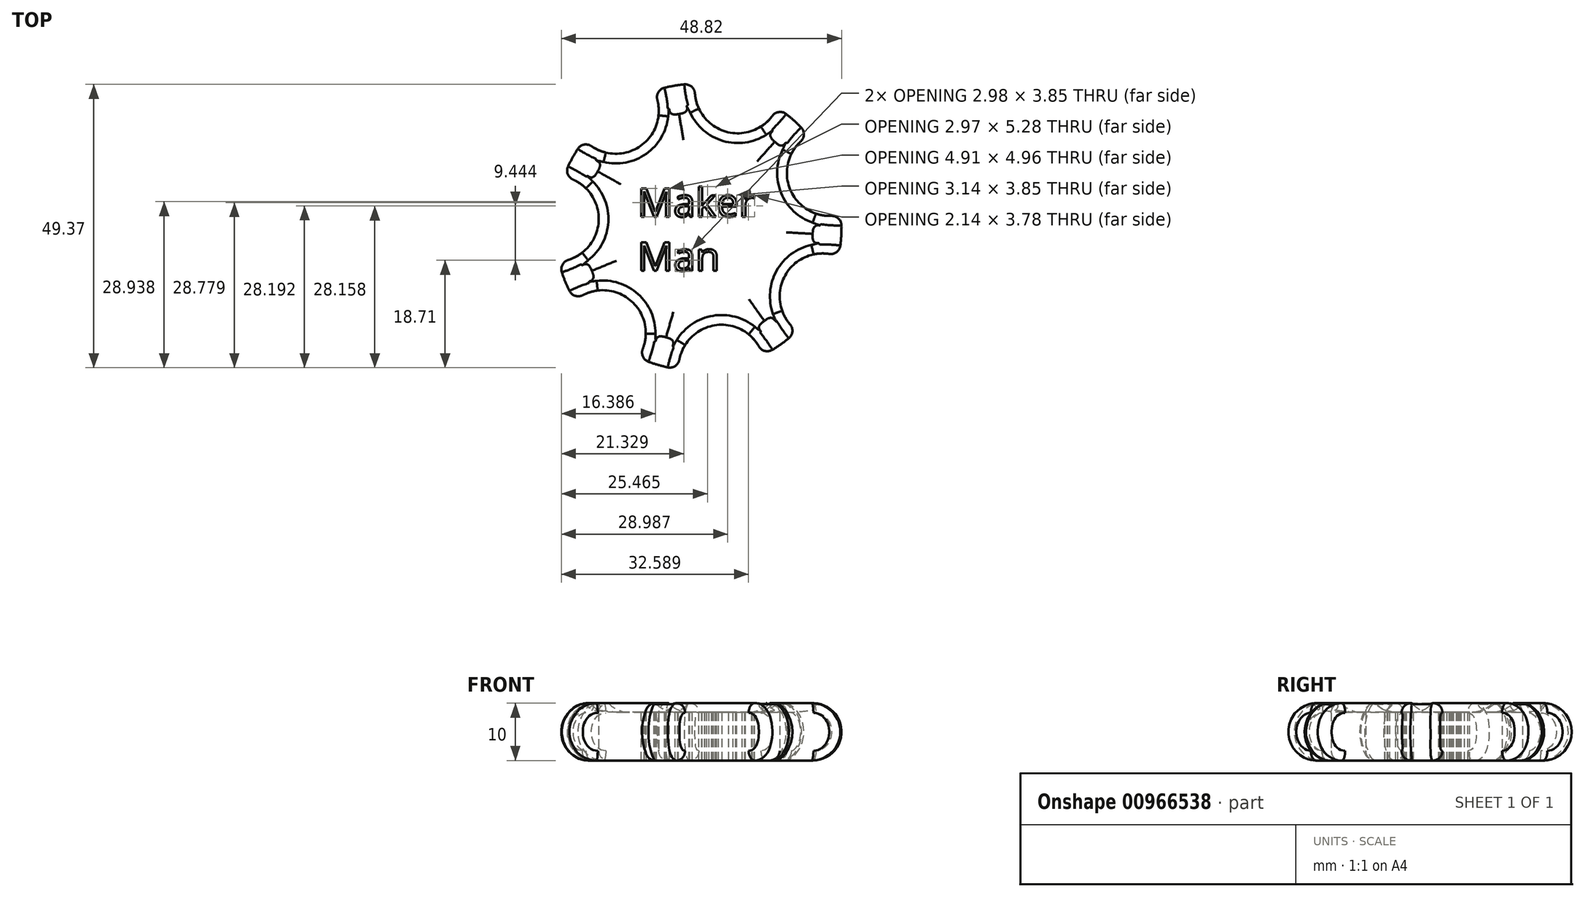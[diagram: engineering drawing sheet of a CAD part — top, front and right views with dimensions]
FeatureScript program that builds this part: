
annotation { "Feature Type Name" : "Feature", "Feature Type Description" : "" }
export const myFeature = defineFeature(function(context is Context, id is Id, definition is map)
    precondition{}
    {
        {
            var Q0;
            Q0=qCreatedBy(makeId("Top.planeOp"),FACE);
            var sketch = newSketch(context, id + "F0", { "sketchPlane" : qUnion([Q0])});
            skCircle(sketch, "E0", {"center": v(0, 0) * mm, "radius": 25 * mm});
            skSolve(sketch);
        }
        {
            var Q0;
            Q0=makeQuery(id+"F0.imprint","IMPRINT",FACE,{"disambiguationData":[TD([[makeQuery(id+"F0.imprint","IMPRINT",EDGE,{"derivedFrom":sQuery(id+"F0.wireOp",EDGE,"E0")}),1.0]])]});
            extrude(context, id + "F1", {"entities" : qUnion([Q0]), "depth" : 10 * mm, "offsetDistance" : 25 * mm});
        }
        {
            var Q0;
            Q0=makeQuery(id+"F1.opExtrude","CAP_EDGE",EDGE,{"disambiguationData":[OSD([sQuery(id+"F0.wireOp",EDGE,"E0")])],"isStart":false});
            var Q1;
            Q1=makeQuery(id+"F1.opExtrude","CAP_EDGE",EDGE,{"disambiguationData":[OSD([sQuery(id+"F0.wireOp",EDGE,"E0")])],"isStart":true});
            fillet(context, id + "F2", {"entities" : qUnion([Q0, Q1]), "radius" : 5 * mm, "tangentPropagation" : true, "allowEdgeOverflow" : false});
        }
        {
            var Q0;
            Q0=qCreatedBy(makeId("Top.planeOp"),FACE);
            var sketch = newSketch(context, id + "F3", { "sketchPlane" : qUnion([Q0])});
            skArc(sketch, "E1", {"start": v(0, 26.67) * mm, "mid": v(5.1, 16.59) * mm, "end": v(14.37, 23.07) * mm});
            skLineSegment(sketch, "E2", {"start": v(14.37, 23.07) * mm, "end": v(0, 26.67) * mm});
            skLineSegment(sketch, "E3.1.0", {"start": v(-9.07, 25.62) * mm, "end": v(-20.85, 16.63) * mm});
            skArc(sketch, "E3.1.1", {"start": v(-20.85, 16.63) * mm, "mid": v(-9.78, 14.33) * mm, "end": v(-9.07, 25.62) * mm});
            skLineSegment(sketch, "E3.2.0", {"start": v(-25.69, 8.88) * mm, "end": v(-26, -5.94) * mm});
            skArc(sketch, "E3.2.1", {"start": v(-26, -5.94) * mm, "mid": v(-17.3, 1.29) * mm, "end": v(-25.69, 8.88) * mm});
            skLineSegment(sketch, "E3.3.0", {"start": v(-22.96, -14.54) * mm, "end": v(-11.57, -24.03) * mm});
            skArc(sketch, "E3.3.1", {"start": v(-11.57, -24.03) * mm, "mid": v(-11.8, -12.73) * mm, "end": v(-22.96, -14.54) * mm});
            skLineSegment(sketch, "E3.4.0", {"start": v(-2.94, -27.02) * mm, "end": v(11.57, -24.03) * mm});
            skArc(sketch, "E3.4.1", {"start": v(11.57, -24.03) * mm, "mid": v(2.6, -17.16) * mm, "end": v(-2.94, -27.02) * mm});
            skLineSegment(sketch, "E3.5.0", {"start": v(19.29, -19.15) * mm, "end": v(26, -5.94) * mm});
            skArc(sketch, "E3.5.1", {"start": v(26, -5.94) * mm, "mid": v(15.03, -8.67) * mm, "end": v(19.29, -19.15) * mm});
            skLineSegment(sketch, "E3.6.0", {"start": v(27, 3.14) * mm, "end": v(20.85, 16.63) * mm});
            skArc(sketch, "E3.6.1", {"start": v(20.85, 16.63) * mm, "mid": v(16.15, 6.35) * mm, "end": v(27, 3.14) * mm});
            skPoint(sketch, "E3.center", {"position": v(0, 0) * mm});
            skSolve(sketch);
        }
        {
            var Q0;
            Q0=makeQuery(id+"F3.imprint","IMPRINT",FACE,{"disambiguationData":[TD([[makeQuery(id+"F3.imprint","IMPRINT",EDGE,{"derivedFrom":sQuery(id+"F3.wireOp",EDGE,"E1")}),1.0]])]});
            extrude(context, id + "F4", {"entities" : qUnion([Q0]), "operationType" : NewBodyOperationType.REMOVE, "depth" : 27.2 * mm, "offsetDistance" : 25 * mm});
        }
        {
            var Q0;
            Q0 = qSketchRegion(id + "F3", true);
            extrude(context, id + "F5", {"entities" : qUnion([Q0]), "operationType" : NewBodyOperationType.REMOVE, "depth" : 25 * mm, "offsetDistance" : 25 * mm});
        }
        {
            var Q0;
            Q0=makeQuery(id+"F4.boolean.opBoolean","COPY",FACE,{"derivedFrom":makeQuery(id+"F4.opExtrude","SWEPT_FACE",FACE,{"disambiguationData":[OSD([sQuery(id+"F3.wireOp",EDGE,"E1")])]})});
            var Q1;
            Q1=makeQuery(id+"F5.boolean.opBoolean","COPY",FACE,{"derivedFrom":makeQuery(id+"F5.opExtrude","SWEPT_FACE",FACE,{"disambiguationData":[OSD([sQuery(id+"F3.wireOp",EDGE,"E3.6.1")])]})});
            var Q2;
            Q2=makeQuery(id+"F5.boolean.opBoolean","COPY",FACE,{"derivedFrom":makeQuery(id+"F5.opExtrude","SWEPT_FACE",FACE,{"disambiguationData":[OSD([sQuery(id+"F3.wireOp",EDGE,"E3.5.1")])]})});
            var Q3;
            Q3=makeQuery(id+"F5.boolean.opBoolean","COPY",FACE,{"derivedFrom":makeQuery(id+"F5.opExtrude","SWEPT_FACE",FACE,{"disambiguationData":[OSD([sQuery(id+"F3.wireOp",EDGE,"E3.4.1")])]})});
            var Q4;
            Q4=makeQuery(id+"F5.boolean.opBoolean","COPY",FACE,{"derivedFrom":makeQuery(id+"F5.opExtrude","SWEPT_FACE",FACE,{"disambiguationData":[OSD([sQuery(id+"F3.wireOp",EDGE,"E3.3.1")])]})});
            var Q5;
            Q5=makeQuery(id+"F5.boolean.opBoolean","COPY",FACE,{"derivedFrom":makeQuery(id+"F5.opExtrude","SWEPT_FACE",FACE,{"disambiguationData":[OSD([sQuery(id+"F3.wireOp",EDGE,"E3.2.1")])]})});
            var Q6;
            Q6=makeQuery(id+"F5.boolean.opBoolean","COPY",FACE,{"derivedFrom":makeQuery(id+"F5.opExtrude","SWEPT_FACE",FACE,{"disambiguationData":[OSD([sQuery(id+"F3.wireOp",EDGE,"E3.1.1")])]})});
            fillet(context, id + "F6", {"entities" : qUnion([Q0, Q1, Q2, Q3, Q4, Q5, Q6]), "radius" : 1.69 * mm, "tangentPropagation" : true, "allowEdgeOverflow" : false});
        }
        {
            var Q0;
            Q0=makeQuery(id+"F1.opExtrude","CAP_FACE",FACE,{"disambiguationData":[OSD([sQuery(id+"F0.wireOp",EDGE,"E0")])],"isStart":false});
            extrude(context, id + "F7", {"entities" : qUnion([Q0]), "operationType" : NewBodyOperationType.REMOVE, "oppositeDirection" : true, "depth" : 1.6 * mm, "offsetDistance" : 25 * mm});
        }
        {
            var Q0;
            Q0=makeQuery(id+"F7.boolean.opBoolean","COPY",FACE,{"derivedFrom":makeQuery(id+"F7.opExtrude","CAP_FACE",FACE,{"disambiguationData":[OSD([sQuery(id+"F0.wireOp",EDGE,"E0")])],"isStart":false})});
            fillet(context, id + "F8", {"entities" : qUnion([Q0]), "radius" : 5 * mm, "tangentPropagation" : true, "allowEdgeOverflow" : false});
        }
        {
            var Q0;
            {var subQ0=sQuery(id+"F0.wireOp",EDGE,"E0");var subQ1=makeQuery(id+"F1.opExtrude","CAP_FACE",FACE,{"disambiguationData":[OSD([subQ0])],"isStart":false});var subQ2=makeQuery(id+"F5.boolean.opBoolean","SPLIT",EDGE,{"disambiguationData":[TD([subQ1,makeQuery(id+"F2.opFillet","BLEND_FACE",FACE,{"disambiguationData":[OSD([subQ0])]}),makeQuery(id+"F4.boolean.opBoolean","COPY",FACE,{"derivedFrom":makeQuery(id+"F4.opExtrude","SWEPT_FACE",FACE,{"disambiguationData":[OSD([sQuery(id+"F3.wireOp",EDGE,"E1")])]})}),makeQuery(id+"F5.opExtrude","SWEPT_FACE",FACE,{"disambiguationData":[OSD([sQuery(id+"F3.wireOp",EDGE,"E3.1.1")])]})])],"derivedFrom":makeQuery(id+"F2.opFillet","BLEND_EDGE",EDGE,{"blendedFrom":[makeQuery(id+"F1.opExtrude","CAP_EDGE",EDGE,{"disambiguationData":[OSD([subQ0])],"isStart":false}),subQ1],"blendedInto":[subQ1]})});Q0=makeQuery(id+"F7.boolean.opBoolean","MERGE",EDGE,{"derivedFrom":[subQ2],"fromTools":[makeQuery(id+"F7.opExtrude","CAP_EDGE",EDGE,{"disambiguationData":[OSD([subQ0]),TDD([subQ2])],"isStart":true})]});}
            var Q1;
            {var subQ0=sQuery(id+"F0.wireOp",EDGE,"E0");var subQ1=makeQuery(id+"F1.opExtrude","CAP_FACE",FACE,{"disambiguationData":[OSD([subQ0])],"isStart":false});var subQ2=makeQuery(id+"F5.boolean.opBoolean","SPLIT",EDGE,{"disambiguationData":[TD([subQ1,makeQuery(id+"F2.opFillet","BLEND_FACE",FACE,{"disambiguationData":[OSD([subQ0])]}),makeQuery(id+"F4.boolean.opBoolean","COPY",FACE,{"derivedFrom":makeQuery(id+"F4.opExtrude","SWEPT_FACE",FACE,{"disambiguationData":[OSD([sQuery(id+"F3.wireOp",EDGE,"E1")])]})}),makeQuery(id+"F5.opExtrude","SWEPT_FACE",FACE,{"disambiguationData":[OSD([sQuery(id+"F3.wireOp",EDGE,"E3.6.1")])]})])],"derivedFrom":makeQuery(id+"F2.opFillet","BLEND_EDGE",EDGE,{"blendedFrom":[makeQuery(id+"F1.opExtrude","CAP_EDGE",EDGE,{"disambiguationData":[OSD([subQ0])],"isStart":false}),subQ1],"blendedInto":[subQ1]})});Q1=makeQuery(id+"F7.boolean.opBoolean","MERGE",EDGE,{"derivedFrom":[subQ2],"fromTools":[makeQuery(id+"F7.opExtrude","CAP_EDGE",EDGE,{"disambiguationData":[OSD([subQ0]),TDD([subQ2])],"isStart":true})]});}
            var Q2;
            {var subQ0=sQuery(id+"F0.wireOp",EDGE,"E0");var subQ1=makeQuery(id+"F1.opExtrude","CAP_FACE",FACE,{"disambiguationData":[OSD([subQ0])],"isStart":false});var subQ2=makeQuery(id+"F5.boolean.opBoolean","SPLIT",EDGE,{"disambiguationData":[TD([subQ1,makeQuery(id+"F2.opFillet","BLEND_FACE",FACE,{"disambiguationData":[OSD([subQ0])]}),makeQuery(id+"F5.opExtrude","SWEPT_FACE",FACE,{"disambiguationData":[OSD([sQuery(id+"F3.wireOp",EDGE,"E3.5.1")])]}),makeQuery(id+"F5.opExtrude","SWEPT_FACE",FACE,{"disambiguationData":[OSD([sQuery(id+"F3.wireOp",EDGE,"E3.6.1")])]})])],"derivedFrom":makeQuery(id+"F2.opFillet","BLEND_EDGE",EDGE,{"blendedFrom":[makeQuery(id+"F1.opExtrude","CAP_EDGE",EDGE,{"disambiguationData":[OSD([subQ0])],"isStart":false}),subQ1],"blendedInto":[subQ1]})});Q2=makeQuery(id+"F7.boolean.opBoolean","MERGE",EDGE,{"derivedFrom":[subQ2],"fromTools":[makeQuery(id+"F7.opExtrude","CAP_EDGE",EDGE,{"disambiguationData":[OSD([subQ0]),TDD([subQ2])],"isStart":true})]});}
            var Q3;
            {var subQ0=sQuery(id+"F0.wireOp",EDGE,"E0");var subQ1=makeQuery(id+"F1.opExtrude","CAP_FACE",FACE,{"disambiguationData":[OSD([subQ0])],"isStart":false});var subQ2=makeQuery(id+"F5.boolean.opBoolean","SPLIT",EDGE,{"disambiguationData":[TD([subQ1,makeQuery(id+"F2.opFillet","BLEND_FACE",FACE,{"disambiguationData":[OSD([subQ0])]}),makeQuery(id+"F5.opExtrude","SWEPT_FACE",FACE,{"disambiguationData":[OSD([sQuery(id+"F3.wireOp",EDGE,"E3.4.1")])]}),makeQuery(id+"F5.opExtrude","SWEPT_FACE",FACE,{"disambiguationData":[OSD([sQuery(id+"F3.wireOp",EDGE,"E3.5.1")])]})])],"derivedFrom":makeQuery(id+"F2.opFillet","BLEND_EDGE",EDGE,{"blendedFrom":[makeQuery(id+"F1.opExtrude","CAP_EDGE",EDGE,{"disambiguationData":[OSD([subQ0])],"isStart":false}),subQ1],"blendedInto":[subQ1]})});Q3=makeQuery(id+"F7.boolean.opBoolean","MERGE",EDGE,{"derivedFrom":[subQ2],"fromTools":[makeQuery(id+"F7.opExtrude","CAP_EDGE",EDGE,{"disambiguationData":[OSD([subQ0]),TDD([subQ2])],"isStart":true})]});}
            var Q4;
            {var subQ0=sQuery(id+"F0.wireOp",EDGE,"E0");var subQ1=makeQuery(id+"F1.opExtrude","CAP_FACE",FACE,{"disambiguationData":[OSD([subQ0])],"isStart":false});var subQ2=makeQuery(id+"F5.boolean.opBoolean","SPLIT",EDGE,{"disambiguationData":[TD([subQ1,makeQuery(id+"F2.opFillet","BLEND_FACE",FACE,{"disambiguationData":[OSD([subQ0])]}),makeQuery(id+"F5.opExtrude","SWEPT_FACE",FACE,{"disambiguationData":[OSD([sQuery(id+"F3.wireOp",EDGE,"E3.3.1")])]}),makeQuery(id+"F5.opExtrude","SWEPT_FACE",FACE,{"disambiguationData":[OSD([sQuery(id+"F3.wireOp",EDGE,"E3.4.1")])]})])],"derivedFrom":makeQuery(id+"F2.opFillet","BLEND_EDGE",EDGE,{"blendedFrom":[makeQuery(id+"F1.opExtrude","CAP_EDGE",EDGE,{"disambiguationData":[OSD([subQ0])],"isStart":false}),subQ1],"blendedInto":[subQ1]})});Q4=makeQuery(id+"F7.boolean.opBoolean","MERGE",EDGE,{"derivedFrom":[subQ2],"fromTools":[makeQuery(id+"F7.opExtrude","CAP_EDGE",EDGE,{"disambiguationData":[OSD([subQ0]),TDD([subQ2])],"isStart":true})]});}
            var Q5;
            {var subQ0=sQuery(id+"F0.wireOp",EDGE,"E0");var subQ1=makeQuery(id+"F1.opExtrude","CAP_FACE",FACE,{"disambiguationData":[OSD([subQ0])],"isStart":false});var subQ2=makeQuery(id+"F5.boolean.opBoolean","SPLIT",EDGE,{"disambiguationData":[TD([subQ1,makeQuery(id+"F2.opFillet","BLEND_FACE",FACE,{"disambiguationData":[OSD([subQ0])]}),makeQuery(id+"F5.opExtrude","SWEPT_FACE",FACE,{"disambiguationData":[OSD([sQuery(id+"F3.wireOp",EDGE,"E3.2.1")])]}),makeQuery(id+"F5.opExtrude","SWEPT_FACE",FACE,{"disambiguationData":[OSD([sQuery(id+"F3.wireOp",EDGE,"E3.3.1")])]})])],"derivedFrom":makeQuery(id+"F2.opFillet","BLEND_EDGE",EDGE,{"blendedFrom":[makeQuery(id+"F1.opExtrude","CAP_EDGE",EDGE,{"disambiguationData":[OSD([subQ0])],"isStart":false}),subQ1],"blendedInto":[subQ1]})});Q5=makeQuery(id+"F7.boolean.opBoolean","MERGE",EDGE,{"derivedFrom":[subQ2],"fromTools":[makeQuery(id+"F7.opExtrude","CAP_EDGE",EDGE,{"disambiguationData":[OSD([subQ0]),TDD([subQ2])],"isStart":true})]});}
            var Q6;
            {var subQ0=sQuery(id+"F0.wireOp",EDGE,"E0");var subQ1=makeQuery(id+"F1.opExtrude","CAP_FACE",FACE,{"disambiguationData":[OSD([subQ0])],"isStart":false});var subQ2=makeQuery(id+"F5.boolean.opBoolean","SPLIT",EDGE,{"disambiguationData":[TD([subQ1,makeQuery(id+"F2.opFillet","BLEND_FACE",FACE,{"disambiguationData":[OSD([subQ0])]}),makeQuery(id+"F5.opExtrude","SWEPT_FACE",FACE,{"disambiguationData":[OSD([sQuery(id+"F3.wireOp",EDGE,"E3.1.1")])]}),makeQuery(id+"F5.opExtrude","SWEPT_FACE",FACE,{"disambiguationData":[OSD([sQuery(id+"F3.wireOp",EDGE,"E3.2.1")])]})])],"derivedFrom":makeQuery(id+"F2.opFillet","BLEND_EDGE",EDGE,{"blendedFrom":[makeQuery(id+"F1.opExtrude","CAP_EDGE",EDGE,{"disambiguationData":[OSD([subQ0])],"isStart":false}),subQ1],"blendedInto":[subQ1]})});Q6=makeQuery(id+"F7.boolean.opBoolean","MERGE",EDGE,{"derivedFrom":[subQ2],"fromTools":[makeQuery(id+"F7.opExtrude","CAP_EDGE",EDGE,{"disambiguationData":[OSD([subQ0]),TDD([subQ2])],"isStart":true})]});}
            fillet(context, id + "F9", {"entities" : qUnion([Q0, Q1, Q2, Q3, Q4, Q5, Q6]), "radius" : 1.1 * mm, "tangentPropagation" : true, "allowEdgeOverflow" : false});
        }
        {
            var Q0;
            Q0=makeQuery(id+"F7.boolean.opBoolean","COPY",FACE,{"derivedFrom":makeQuery(id+"F7.opExtrude","CAP_FACE",FACE,{"disambiguationData":[OSD([sQuery(id+"F0.wireOp",EDGE,"E0")])],"isStart":false})});
            var sketch = newSketch(context, id + "F10", { "sketchPlane" : qUnion([Q0])});
            skText(sketch, "E4", { "text": "Maker \nMan", "fontName": "OpenSans-Regular.ttf"});
            const initialGuessF10  = {"E4": [-0.01057, 0.00182, 1, 0, 0.005]};
            skSetInitialGuess(sketch, initialGuessF10);
            skSolve(sketch);
        }
        {
            var Q0;
            Q0 = qSketchRegion(id + "F10", true);
            extrude(context, id + "F11", {"entities" : qUnion([Q0]), "operationType" : NewBodyOperationType.REMOVE, "oppositeDirection" : true, "depth" : 25 * mm, "offsetDistance" : 25 * mm});
        }
    });
